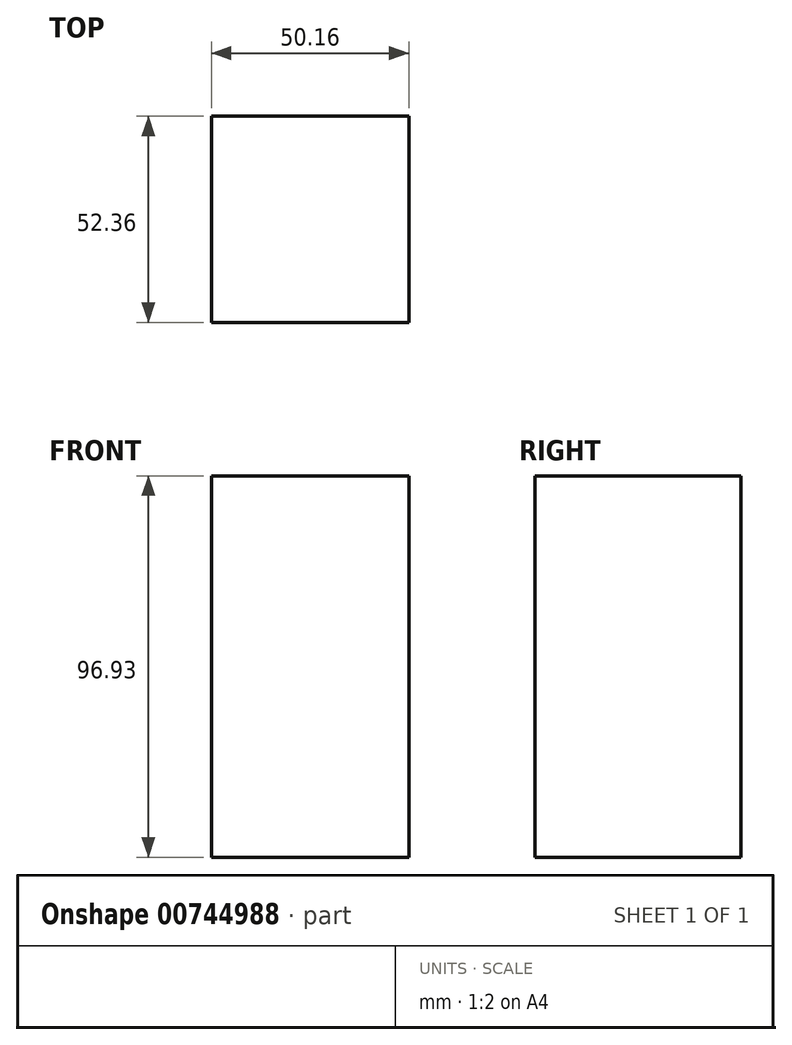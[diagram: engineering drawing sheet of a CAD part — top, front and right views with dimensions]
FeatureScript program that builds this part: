
annotation { "Feature Type Name" : "Feature", "Feature Type Description" : "" }
export const myFeature = defineFeature(function(context is Context, id is Id, definition is map)
    precondition{}
    {
        {
            var Q0;
            Q0=qCreatedBy(makeId("Top.planeOp"),FACE);
            var sketch = newSketch(context, id + "F0", { "sketchPlane" : qUnion([Q0])});
            skLineSegment(sketch, "E0.bottom", {"start": v(50.16, -33.64) * mm, "end": v(0, -33.64) * mm});
            skLineSegment(sketch, "E0.top", {"start": v(50.16, 18.72) * mm, "end": v(0, 18.72) * mm});
            skLineSegment(sketch, "E0.left", {"start": v(50.16, -33.64) * mm, "end": v(50.16, 18.72) * mm});
            skLineSegment(sketch, "E0.right", {"start": v(0, -33.64) * mm, "end": v(0, 18.72) * mm});
            skSolve(sketch);
        }
        {
            var Q0;
            Q0 = qSketchRegion(id + "F0", true);
            var Q1;
            Q1=makeQuery(id+"F0.imprint","IMPRINT",FACE,{"disambiguationData":[TD([[makeQuery(id+"F0.imprint","IMPRINT",EDGE,{"derivedFrom":sQuery(id+"F0.wireOp",EDGE,"E0.bottom")}),-1.0]])]});
            extrude(context, id + "F1", {"entities" : qUnion([Q0, Q1]), "depth" : 96.93 * mm, "offsetDistance" : 25.4 * mm});
        }
    });
